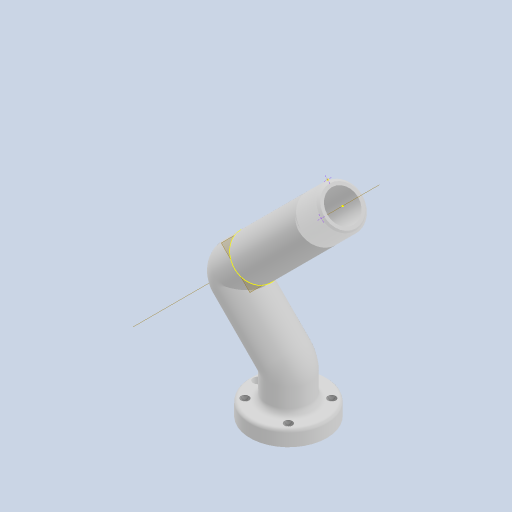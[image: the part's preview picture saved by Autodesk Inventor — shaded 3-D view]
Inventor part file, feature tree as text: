
AUTODESK INVENTOR PART (.ipt)
format: ipt  version: 2023 (Build 270158000, 158)  size: 307,200 bytes
history: native  units: in
note: dims shown in document units (in); Inventor stores cm internally (conversion verified against a paired STEP export)
features: sketch x11, plane x4, extrude x3, fillet x2, sweep x1, hole x1, chamfer x1, other x1, helix x1
ambient origin geometry x8: Origin, YZ Plane, XZ Plane, XY Plane, X Axis, Y Axis, Z Axis, Center Point
bodies: Body1 (feature_tree)
feature tree (25):
  plane  "Work Plane1"
  sweep  "Sweep2"
  extrude  "Extrusion1"  TaperAngle=90.0deg  [1 undecoded]
  hole  "Hole1"  [1 undecoded]
  fillet  "Fillet1"  [1 undecoded]
  fillet  "Fillet2"  Radius=0.7874in
  sketch  "Sketch7"  dims[d18=0.3937in]
  sketch  "Sketch9"  dims[d19=1.9685in]
  plane  "Work Plane3"
  plane  "Work Plane4"
  sketch  "Sketch11"  dims[d20=1.5748in]
  sketch  "Sketch12"  dims[d21=0.2362in]
  chamfer  "Chamfer1"  Distance=1.5748in Angle=360.0deg
  plane  "Work Plane6"
  sketch  "Sketch15"  dims[d22=45.0deg]
  other  "Work Axis1"
  helix  "Coil1"  [1 undecoded]
  extrude  "Extrusion3"  Depth=0.0787in
  extrude  "Extrusion6"  TaperAngle=45.0deg  [1 undecoded]
  sketch  "Sketch20"  dims[d38=0.0787in d58=45.0deg d59=-3.1496in d63=0.0787in d64=0.0787in d65=45.0deg d67=0.0787in d68=0.0787in d69=0.7874in d70=0.3937in d71=0.0in d72=90.0deg d73=90.0deg d74=0.0in d75=0.0in d76=0.3937in d77=0.0in d92=0.7874in d93=3.3465in d94=0.0in d39=0.0in d40=0.0in d41=0.0in]
  sketch  "Sketch4"  dims[d5=3.937in d6=135.0deg]
  sketch  "Sketch5"  dims[d7=1.9685in d8=90.0deg]
  sketch  "Sketch6"  dims[d9=0.1969in d13=1.1024in d14=0.0in d15=0.0in d17=0.7874in]
  sketch  "Sketch16"  dims[d23=0.1969in d24=1.5748in d26=360.0deg d28=0.3937in d29=0.0in]
  sketch  "Sketch19"  dims[d30=0.2064in d31=0.4724in d32=0.1575in d33=0.0787in d34=90.0deg d35=0.622in d36=120.0deg d37=0.1575in]
note: 5 required parameter values undecoded (feature->parameter linkage not recoverable at this tier; creation-order binding heuristic only, values carry confidence <= 0.55)
